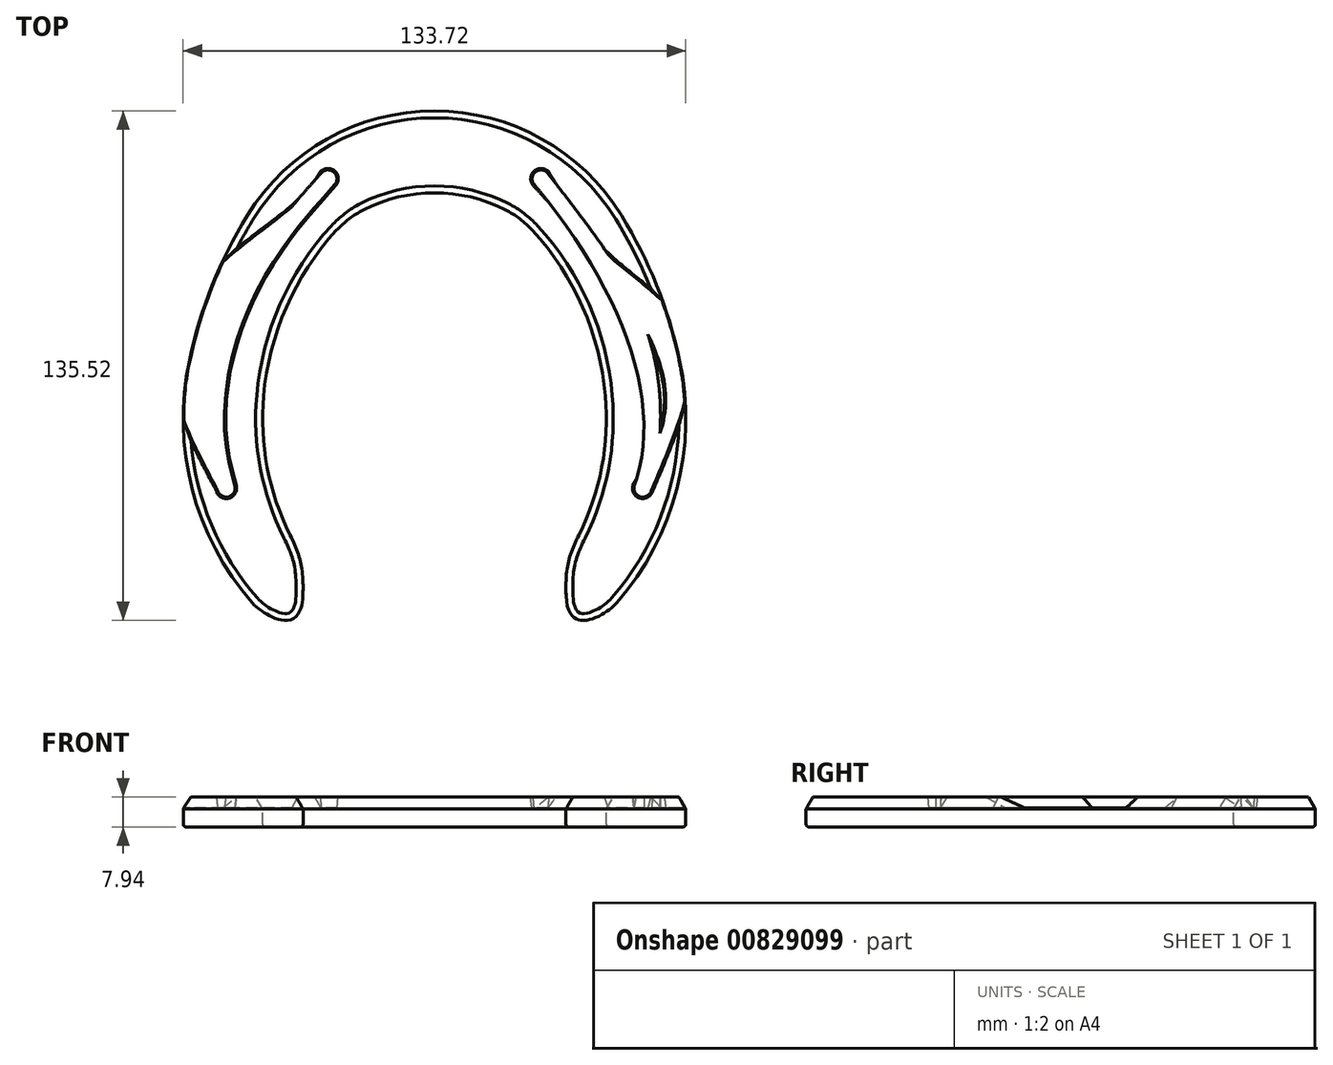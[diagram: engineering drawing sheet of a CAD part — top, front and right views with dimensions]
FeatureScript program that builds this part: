
annotation { "Feature Type Name" : "Feature", "Feature Type Description" : "" }
export const myFeature = defineFeature(function(context is Context, id is Id, definition is map)
    precondition{}
    {
        {
            var Q0;
            Q0=qCreatedBy(makeId("Top.planeOp"),FACE);
            var sketch = newSketch(context, id + "F0", { "sketchPlane" : qUnion([Q0])});
            skLineSegment(sketch, "E0", {"start": v(-63.98, 0) * mm, "end": v(70.39, 0) * mm, "construction": true});
            skLineSegment(sketch, "E1", {"start": v(70.39, 15.7) * mm, "end": v(70.39, -30.4) * mm, "construction": true});
            skLineSegment(sketch, "E2", {"start": v(-63.98, 15.94) * mm, "end": v(-63.98, -30.4) * mm, "construction": true});
            skPoint(sketch, "E3.orphan", {"position": v(-62.69, 0) * mm});
            skPoint(sketch, "E4.orphan", {"position": v(69.71, 0) * mm});
            skSolve(sketch);
        }
        {
            var Q0;
            Q0=qCreatedBy(makeId("Top.planeOp"),FACE);
            var sketch = newSketch(context, id + "F1", { "sketchPlane" : qUnion([Q0])});
            skArc(sketch, "E5", {"start": v(-46.57, 47.97) * mm, "mid": v(-55.91, 29.42) * mm, "end": v(-62, 9.55) * mm});
            skArc(sketch, "E6", {"start": v(-62, 9.55) * mm, "mid": v(-61.3, -24.7) * mm, "end": v(-45.33, -55) * mm});
            skLineSegment(sketch, "E7.0", {"start": v(-63.98, 15.94) * mm, "end": v(-63.98, -30.4) * mm, "construction": true});
            skLineSegment(sketch, "E8.0", {"start": v(70.39, 15.7) * mm, "end": v(70.39, -30.4) * mm, "construction": true});
            skLineSegment(sketch, "E9", {"start": v(70.39, -26.25) * mm, "end": v(-63.98, -26.25) * mm, "construction": true});
            skLineSegment(sketch, "E10", {"start": v(3.2, -29.11) * mm, "end": v(3.2, -21.5) * mm, "construction": true});
            skArc(sketch, "E11.MirrorCS", {"start": v(68.4, 9.55) * mm, "mid": v(67.7, -24.7) * mm, "end": v(51.73, -55) * mm});
            skArc(sketch, "E12.MirrorCS", {"start": v(52.98, 47.97) * mm, "mid": v(62.32, 29.42) * mm, "end": v(68.4, 9.55) * mm});
            skArc(sketch, "E13", {"start": v(52.98, 47.97) * mm, "mid": v(3.2, 75.8) * mm, "end": v(-46.57, 47.97) * mm});
            skArc(sketch, "E14", {"start": v(-42.27, 0) * mm, "mid": v(-41.31, -18.96) * mm, "end": v(-35.25, -36.96) * mm});
            skArc(sketch, "E15", {"start": v(-22.9, 44.02) * mm, "mid": v(-36.22, 23.61) * mm, "end": v(-42.27, 0) * mm});
            skArc(sketch, "E16.MirrorCS", {"start": v(48.67, 0) * mm, "mid": v(47.72, -18.96) * mm, "end": v(41.65, -36.96) * mm});
            skArc(sketch, "E17.MirrorCS", {"start": v(29.3, 44.02) * mm, "mid": v(42.62, 23.61) * mm, "end": v(48.67, 0) * mm});
            skFitSpline(sketch, "E18", {"points": [v(-35.25, -36.96) * mm, v(-31.82, -53.27) * mm], "startDerivative": vector(8.24, -16.52) * mm, "endDerivative": vector(-0.9, -22.38) * mm});
            skFitSpline(sketch, "E19", {"points": [v(-45.33, -55) * mm, v(-31.82, -53.27) * mm], "startDerivative": vector(8.37, -9.6) * mm, "endDerivative": vector(1.36, 34.08) * mm});
            skFitSpline(sketch, "E20.MirrorCS", {"points": [v(51.73, -55) * mm, v(38.22, -53.27) * mm], "startDerivative": vector(-8.37, -9.6) * mm, "endDerivative": vector(-1.36, 34.08) * mm});
            skFitSpline(sketch, "E21.MirrorCS", {"points": [v(41.65, -36.96) * mm, v(38.22, -53.27) * mm], "startDerivative": vector(-8.24, -16.52) * mm, "endDerivative": vector(0.9, -22.38) * mm});
            skLineSegment(sketch, "E22.MirrorCS", {"start": v(70.39, 15.94) * mm, "end": v(70.39, -30.4) * mm});
            skLineSegment(sketch, "E23.MirrorCS", {"start": v(-63.98, 15.7) * mm, "end": v(-63.98, -30.4) * mm});
            skArc(sketch, "E24", {"start": v(22.05, 49.51) * mm, "mid": v(3.2, 54.01) * mm, "end": v(-15.65, 49.51) * mm});
            skPoint(sketch, "E25.visualSharp", {"position": v(-20.12, 46.89) * mm});
            skArc(sketch, "E25.filletArc", {"start": v(-15.65, 49.51) * mm, "mid": v(-19.52, 47.1) * mm, "end": v(-22.9, 44.02) * mm});
            skPoint(sketch, "E26.visualSharp", {"position": v(26.52, 46.89) * mm});
            skArc(sketch, "E26.filletArc", {"start": v(29.3, 44.02) * mm, "mid": v(25.92, 47.1) * mm, "end": v(22.05, 49.51) * mm});
            skSolve(sketch);
        }
        {
            var Q0;
            Q0 = qSketchRegion(id + "F1", true);
            extrude(context, id + "F2", {"entities" : qUnion([Q0]), "oppositeDirection" : true, "depth" : 7.94 * mm, "offsetDistance" : 25.4 * mm});
        }
        {
            var Q0;
            Q0=makeQuery(id+"F2.opExtrude","CAP_EDGE",EDGE,{"disambiguationData":[OSD([sQuery(id+"F1.wireOp",EDGE,"E15")])],"isStart":true});
            chamfer(context, id + "F3", {"entities" : qUnion([Q0]), "chamferType" : ChamferType.OFFSET_ANGLE, "width" : 3.17 * mm, "oppositeDirection" : false, "angle" : 30 * degree, "tangentPropagation" : true});
        }
        {
            var Q0;
            Q0=makeQuery(id+"F2.opExtrude","CAP_FACE",FACE,{"disambiguationData":[OSD([sQuery(id+"F1.wireOp",EDGE,"E5"),sQuery(id+"F1.wireOp",EDGE,"E6"),sQuery(id+"F1.wireOp",EDGE,"E11.MirrorCS"),sQuery(id+"F1.wireOp",EDGE,"E12.MirrorCS"),sQuery(id+"F1.wireOp",EDGE,"E13"),sQuery(id+"F1.wireOp",EDGE,"E14"),sQuery(id+"F1.wireOp",EDGE,"E15"),sQuery(id+"F1.wireOp",EDGE,"E16.MirrorCS"),sQuery(id+"F1.wireOp",EDGE,"E17.MirrorCS"),sQuery(id+"F1.wireOp",EDGE,"E18"),sQuery(id+"F1.wireOp",EDGE,"E19"),sQuery(id+"F1.wireOp",EDGE,"E20.MirrorCS"),sQuery(id+"F1.wireOp",EDGE,"E21.MirrorCS"),sQuery(id+"F1.wireOp",EDGE,"E24"),sQuery(id+"F1.wireOp",EDGE,"E25.filletArc"),sQuery(id+"F1.wireOp",EDGE,"E26.filletArc")])],"isStart":false});
            fillet(context, id + "F4", {"entities" : qUnion([Q0]), "radius" : 0.76 * mm, "tangentPropagation" : true, "allowEdgeOverflow" : false});
        }
        {
            var Q0;
            Q0=makeQuery(id+"F2.opExtrude","CAP_FACE",FACE,{"disambiguationData":[OSD([sQuery(id+"F1.wireOp",EDGE,"E5"),sQuery(id+"F1.wireOp",EDGE,"E6"),sQuery(id+"F1.wireOp",EDGE,"E11.MirrorCS"),sQuery(id+"F1.wireOp",EDGE,"E12.MirrorCS"),sQuery(id+"F1.wireOp",EDGE,"E13"),sQuery(id+"F1.wireOp",EDGE,"E14"),sQuery(id+"F1.wireOp",EDGE,"E15"),sQuery(id+"F1.wireOp",EDGE,"E16.MirrorCS"),sQuery(id+"F1.wireOp",EDGE,"E17.MirrorCS"),sQuery(id+"F1.wireOp",EDGE,"E18"),sQuery(id+"F1.wireOp",EDGE,"E19"),sQuery(id+"F1.wireOp",EDGE,"E20.MirrorCS"),sQuery(id+"F1.wireOp",EDGE,"E21.MirrorCS"),sQuery(id+"F1.wireOp",EDGE,"E24"),sQuery(id+"F1.wireOp",EDGE,"E25.filletArc"),sQuery(id+"F1.wireOp",EDGE,"E26.filletArc")])],"isStart":true});
            var sketch = newSketch(context, id + "F5", { "sketchPlane" : qUnion([Q0])});
            skFitSpline(sketch, "E27", {"points": [v(-54.5, -25.15) * mm, v(-26.93, 59.3) * mm], "startDerivative": vector(-33.9, 133.5) * mm, "endDerivative": vector(23.31, 27.01) * mm});
            skFitSpline(sketch, "E28.0", {"points": [v(-49.9, -23.98) * mm, v(-51.23, -18.74) * mm, v(-52.64, -8.7) * mm, v(-51.74, 5.04) * mm, v(-48.56, 17.46) * mm, v(-43.78, 28.49) * mm, v(-38.1, 38.01) * mm, v(-33.25, 44.6) * mm, v(-29.65, 49) * mm, v(-27.18, 51.86) * mm, v(-25.03, 54.28) * mm, v(-23.85, 55.6) * mm, v(-23.33, 56.2) * mm]});
            skArc(sketch, "E29", {"start": v(-23.33, 56.2) * mm, "mid": v(-23.58, 59.55) * mm, "end": v(-26.93, 59.3) * mm});
            skArc(sketch, "E30", {"start": v(-54.5, -25.15) * mm, "mid": v(-51.62, -26.87) * mm, "end": v(-49.9, -23.98) * mm});
            skLineSegment(sketch, "E31.0", {"start": v(-63.98, 15.94) * mm, "end": v(-63.98, -30.4) * mm, "construction": true});
            skLineSegment(sketch, "E32.0", {"start": v(70.39, 15.7) * mm, "end": v(70.39, -30.4) * mm, "construction": true});
            skLineSegment(sketch, "E33", {"start": v(70.39, -25.15) * mm, "end": v(-63.98, -25.15) * mm, "construction": true});
            skLineSegment(sketch, "E34", {"start": v(3.2, -25.15) * mm, "end": v(3.2, 9.62) * mm, "construction": true});
            skArc(sketch, "E35.MirrorCS", {"start": v(60.9, -25.15) * mm, "mid": v(58.02, -26.87) * mm, "end": v(56.3, -23.98) * mm});
            skArc(sketch, "E36.MirrorCS", {"start": v(29.74, 56.2) * mm, "mid": v(29.98, 59.55) * mm, "end": v(33.33, 59.3) * mm});
            skFitSpline(sketch, "E37", {"points": [v(29.74, 56.2) * mm, v(56.3, -23.98) * mm], "startDerivative": vector(66.55, -79.2) * mm, "endDerivative": vector(-25.29, -69.86) * mm});
            skFitSpline(sketch, "E38", {"points": [v(33.33, 59.3) * mm, v(60.9, -25.15) * mm], "startDerivative": vector(50.88, -67.8) * mm, "endDerivative": vector(-28.43, -122.55) * mm});
            skSolve(sketch);
        }
        {
            var Q0;
            Q0 = qSketchRegion(id + "F5", true);
            extrude(context, id + "F6", {"entities" : qUnion([Q0]), "operationType" : NewBodyOperationType.REMOVE, "oppositeDirection" : true, "depth" : 2.95 * mm, "offsetDistance" : 25.4 * mm});
        }
        {
            var Q0;
            Q0=makeQuery(id+"F6.boolean.opBoolean","COPY",FACE,{"derivedFrom":makeQuery(id+"F6.opExtrude","CAP_FACE",FACE,{"disambiguationData":[OSD([sQuery(id+"F5.wireOp",EDGE,"E27"),sQuery(id+"F5.wireOp",EDGE,"E28.0"),sQuery(id+"F5.wireOp",EDGE,"E29"),sQuery(id+"F5.wireOp",EDGE,"E30")])],"isStart":false})});
            var sketch = newSketch(context, id + "F7", { "sketchPlane" : qUnion([Q0])});
            skArc(sketch, "E39.0.0", {"start": v(-54.5, -25.15) * mm, "mid": v(-51.62, -26.87) * mm, "end": v(-49.9, -23.98) * mm});
            skFitSpline(sketch, "E39.0.1", {"points": [v(-49.9, -23.98) * mm, v(-51.23, -18.74) * mm, v(-52.64, -8.7) * mm, v(-51.74, 5.04) * mm, v(-48.56, 17.46) * mm, v(-43.78, 28.49) * mm, v(-38.1, 38.01) * mm, v(-33.25, 44.6) * mm, v(-29.65, 49) * mm, v(-27.18, 51.86) * mm, v(-25.03, 54.28) * mm, v(-23.85, 55.6) * mm, v(-23.33, 56.2) * mm]});
            skArc(sketch, "E39.0.2", {"start": v(-23.33, 56.2) * mm, "mid": v(-23.58, 59.55) * mm, "end": v(-26.93, 59.3) * mm});
            skFitSpline(sketch, "E39.0.3", {"points": [v(-26.93, 59.3) * mm, v(-34.7, 50.3) * mm, v(-65.8, 19.35) * mm, v(-54.5, -25.15) * mm]});
            skArc(sketch, "E40.0.0", {"start": v(33.33, 59.3) * mm, "mid": v(29.98, 59.55) * mm, "end": v(29.74, 56.2) * mm});
            skFitSpline(sketch, "E40.0.1", {"points": [v(29.74, 56.2) * mm, v(51.92, 29.8) * mm, v(64.73, -0.7) * mm, v(56.3, -23.98) * mm]});
            skArc(sketch, "E40.0.2", {"start": v(56.3, -23.98) * mm, "mid": v(58.02, -26.87) * mm, "end": v(60.9, -25.15) * mm});
            skFitSpline(sketch, "E40.0.3", {"points": [v(60.9, -25.15) * mm, v(70.39, 15.7) * mm, v(50.3, 36.7) * mm, v(33.33, 59.3) * mm]});
            skSolve(sketch);
        }
        {
            var Q0;
            Q0 = qSketchRegion(id + "F7", true);
            extrude(context, id + "F8", {"entities" : qUnion([Q0]), "operationType" : NewBodyOperationType.REMOVE, "depth" : 25.4 * mm, "offsetDistance" : 25.4 * mm, "hasDraft" : true, "draftAngle" : 7 * degree});
        }
    });
